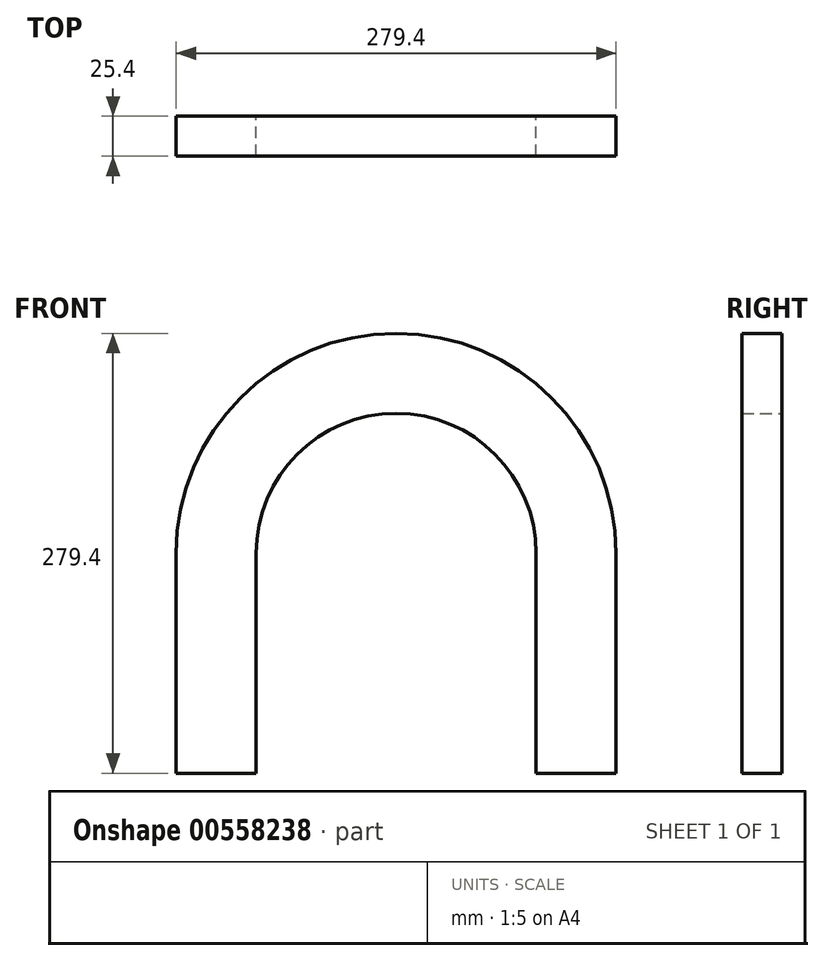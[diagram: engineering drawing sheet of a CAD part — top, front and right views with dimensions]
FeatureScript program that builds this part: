
annotation { "Feature Type Name" : "Feature", "Feature Type Description" : "" }
export const myFeature = defineFeature(function(context is Context, id is Id, definition is map)
    precondition{}
    {
        {
            var Q0;
            Q0=qCreatedBy(makeId("Front.planeOp"),FACE);
            var sketch = newSketch(context, id + "F0", { "sketchPlane" : qUnion([Q0])});
            skArc(sketch, "E0", {"start": v(139.7, 0) * mm, "mid": v(0, 139.7) * mm, "end": v(-139.7, 0) * mm});
            skArc(sketch, "E1", {"start": v(88.9, 0) * mm, "mid": v(0, 88.9) * mm, "end": v(-88.9, 0) * mm});
            skLineSegment(sketch, "E2", {"start": v(-139.7, 0) * mm, "end": v(-139.7, -139.7) * mm});
            skLineSegment(sketch, "E3", {"start": v(-139.7, -139.7) * mm, "end": v(-88.9, -139.7) * mm});
            skLineSegment(sketch, "E4", {"start": v(-88.9, -139.7) * mm, "end": v(-88.9, 0) * mm});
            skLineSegment(sketch, "E5", {"start": v(139.7, 0) * mm, "end": v(139.7, -139.7) * mm});
            skLineSegment(sketch, "E6", {"start": v(139.7, -139.7) * mm, "end": v(88.9, -139.7) * mm});
            skLineSegment(sketch, "E7", {"start": v(88.9, -139.7) * mm, "end": v(88.9, 0) * mm});
            skSolve(sketch);
        }
        {
            var Q0;
            Q0 = qSketchRegion(id + "F0", true);
            extrude(context, id + "F1", {"entities" : qUnion([Q0]), "depth" : 25.4 * mm, "offsetDistance" : 25.4 * mm});
        }
    });
